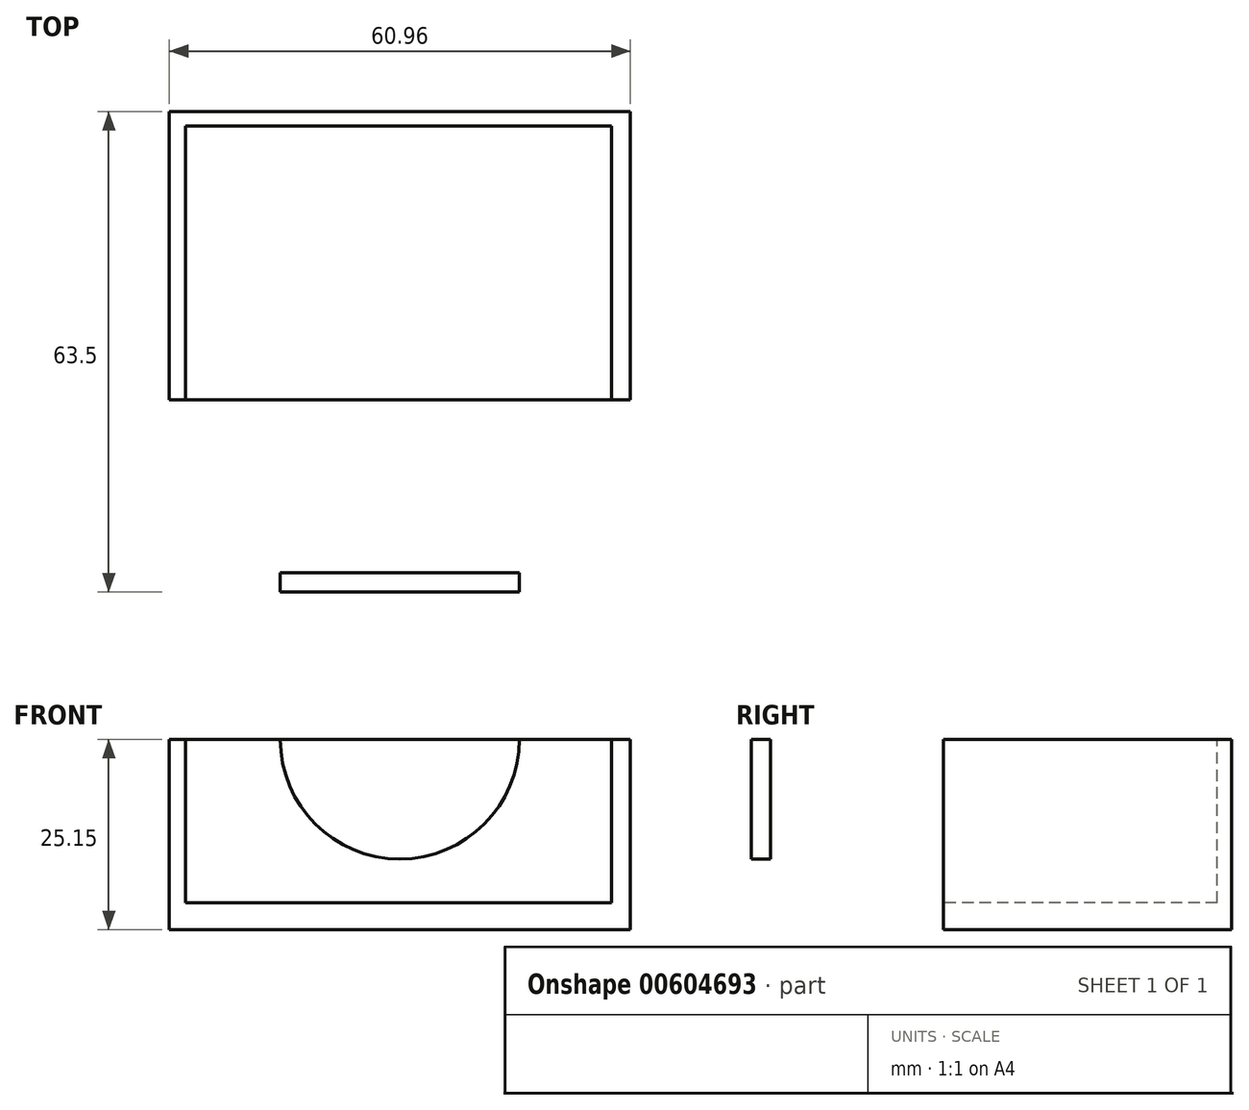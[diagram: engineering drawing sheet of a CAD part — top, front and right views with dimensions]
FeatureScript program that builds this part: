
annotation { "Feature Type Name" : "Feature", "Feature Type Description" : "" }
export const myFeature = defineFeature(function(context is Context, id is Id, definition is map)
    precondition{}
    {
        {
            var Q0;
            Q0=qCreatedBy(makeId("Top.planeOp"),FACE);
            var sketch = newSketch(context, id + "F0", { "sketchPlane" : qUnion([Q0])});
            skLineSegment(sketch, "E0.bottom", {"start": v(0, 0) * mm, "end": v(60.96, 0) * mm});
            skLineSegment(sketch, "E0.top", {"start": v(0, 63.5) * mm, "end": v(60.96, 63.5) * mm});
            skLineSegment(sketch, "E0.left", {"start": v(0, 0) * mm, "end": v(0, 63.5) * mm});
            skLineSegment(sketch, "E0.right", {"start": v(60.96, 0) * mm, "end": v(60.96, 63.5) * mm});
            skSolve(sketch);
        }
        {
            var Q0;
            Q0=makeQuery(id+"F0.imprint","IMPRINT",FACE,{"disambiguationData":[TD([[makeQuery(id+"F0.imprint","IMPRINT",EDGE,{"derivedFrom":sQuery(id+"F0.wireOp",EDGE,"E0.bottom")}),1.0]])]});
            extrude(context, id + "F1", {"entities" : qUnion([Q0]), "depth" : 25.15 * mm, "offsetDistance" : 25.4 * mm});
        }
        {
            var Q0;
            Q0=makeQuery(id+"F1.opExtrude","CAP_FACE",FACE,{"disambiguationData":[OSD([sQuery(id+"F0.wireOp",EDGE,"E0.bottom"),sQuery(id+"F0.wireOp",EDGE,"E0.top"),sQuery(id+"F0.wireOp",EDGE,"E0.left"),sQuery(id+"F0.wireOp",EDGE,"E0.right")])],"isStart":false});
            var sketch = newSketch(context, id + "F2", { "sketchPlane" : qUnion([Q0])});
            skLineSegment(sketch, "E1.bottom", {"start": v(2.13, 61.57) * mm, "end": v(58.44, 61.57) * mm});
            skLineSegment(sketch, "E1.top", {"start": v(2.13, 2.55) * mm, "end": v(58.44, 2.55) * mm});
            skLineSegment(sketch, "E1.left", {"start": v(2.13, 61.57) * mm, "end": v(2.13, 2.55) * mm});
            skLineSegment(sketch, "E1.right", {"start": v(58.44, 61.57) * mm, "end": v(58.44, 2.55) * mm});
            skSolve(sketch);
        }
        {
            var Q0;
            Q0=makeQuery(id+"F2.imprint","IMPRINT",FACE,{"disambiguationData":[TD([[makeQuery(id+"F2.imprint","IMPRINT",EDGE,{"derivedFrom":sQuery(id+"F2.wireOp",EDGE,"E1.bottom")}),-1.0]])]});
            extrude(context, id + "F3", {"entities" : qUnion([Q0]), "operationType" : NewBodyOperationType.REMOVE, "oppositeDirection" : true, "depth" : 21.59 * mm, "offsetDistance" : 25.4 * mm});
        }
        {
            var Q0;
            Q0=makeQuery(id+"F1.opExtrude","SWEPT_FACE",FACE,{"disambiguationData":[OSD([sQuery(id+"F0.wireOp",EDGE,"E0.bottom")])]});
            var sketch = newSketch(context, id + "F4", { "sketchPlane" : qUnion([Q0])});
            skArc(sketch, "E2", {"start": v(46.28, 25.15) * mm, "mid": v(30.48, 9.35) * mm, "end": v(14.68, 25.15) * mm});
            skSolve(sketch);
        }
        {
            var Q0;
            {var subQ0=sQuery(id+"F4.wireOp",EDGE,"E2");Q0=makeQuery(id+"F4.imprint","IMPRINT",FACE,{"disambiguationData":[TD([[makeQuery(id+"F4.imprint","IMPRINT",EDGE,{"derivedFrom":subQ0}),-1.0]])]});}
            extrude(context, id + "F5", {"entities" : qUnion([Q0]), "operationType" : NewBodyOperationType.REMOVE, "oppositeDirection" : true, "depth" : 25.4 * mm, "offsetDistance" : 25.4 * mm});
        }
    });
